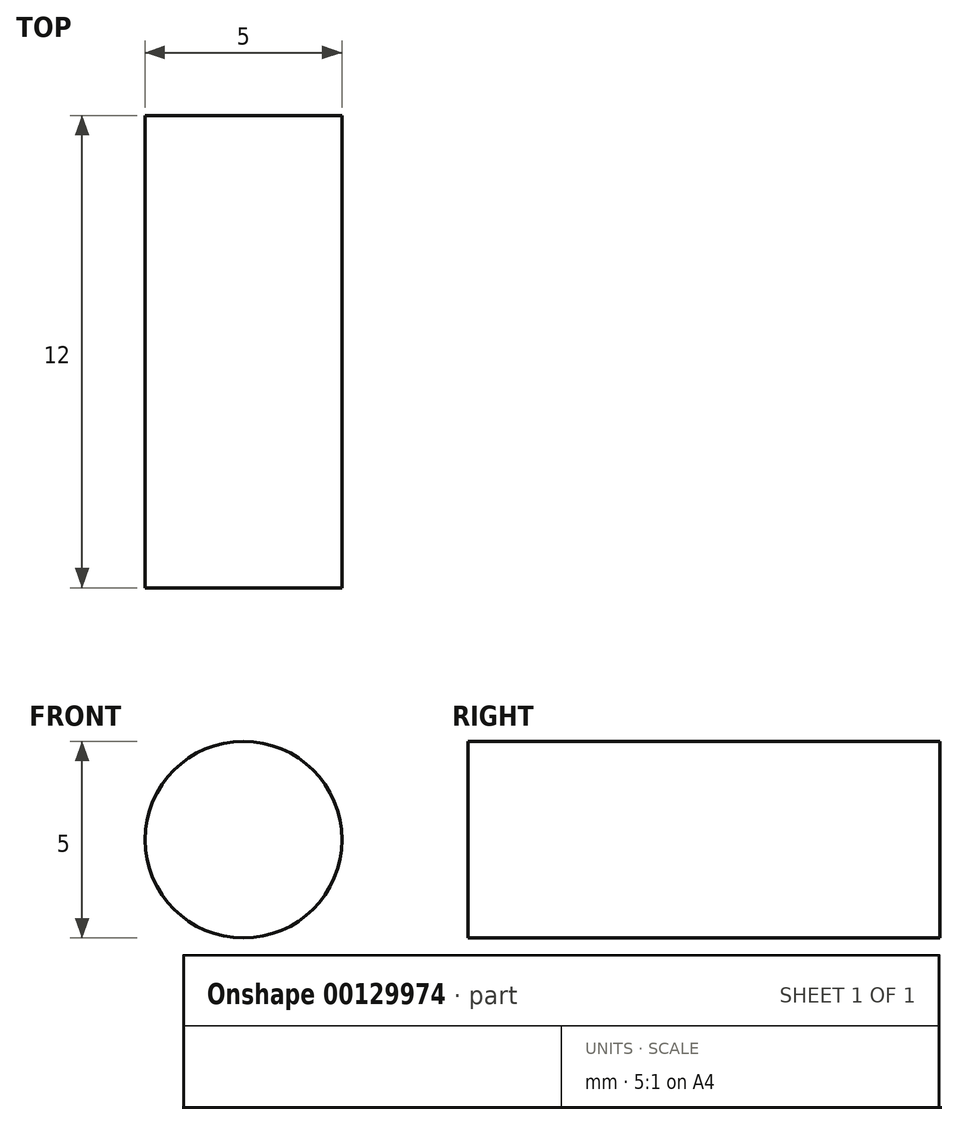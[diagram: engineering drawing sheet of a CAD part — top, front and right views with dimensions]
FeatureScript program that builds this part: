
annotation { "Feature Type Name" : "Feature", "Feature Type Description" : "" }
export const myFeature = defineFeature(function(context is Context, id is Id, definition is map)
    precondition{}
    {
        {
            var Q0;
            Q0=qCreatedBy(makeId("Front.planeOp"),FACE);
            var sketch = newSketch(context, id + "F0", { "sketchPlane" : qUnion([Q0])});
            skCircle(sketch, "E0", {"center": v(0, 0) * mm, "radius": 2.5 * mm});
            skSolve(sketch);
        }
        {
            var Q0;
            Q0=makeQuery(id+"F0.imprint","IMPRINT",FACE,{"disambiguationData":[TD([[makeQuery(id+"F0.imprint","IMPRINT",EDGE,{"derivedFrom":sQuery(id+"F0.wireOp",EDGE,"E0")}),1.0]])]});
            extrude(context, id + "F1", {"entities" : qUnion([Q0]), "depth" : 12 * mm});
        }
    });
